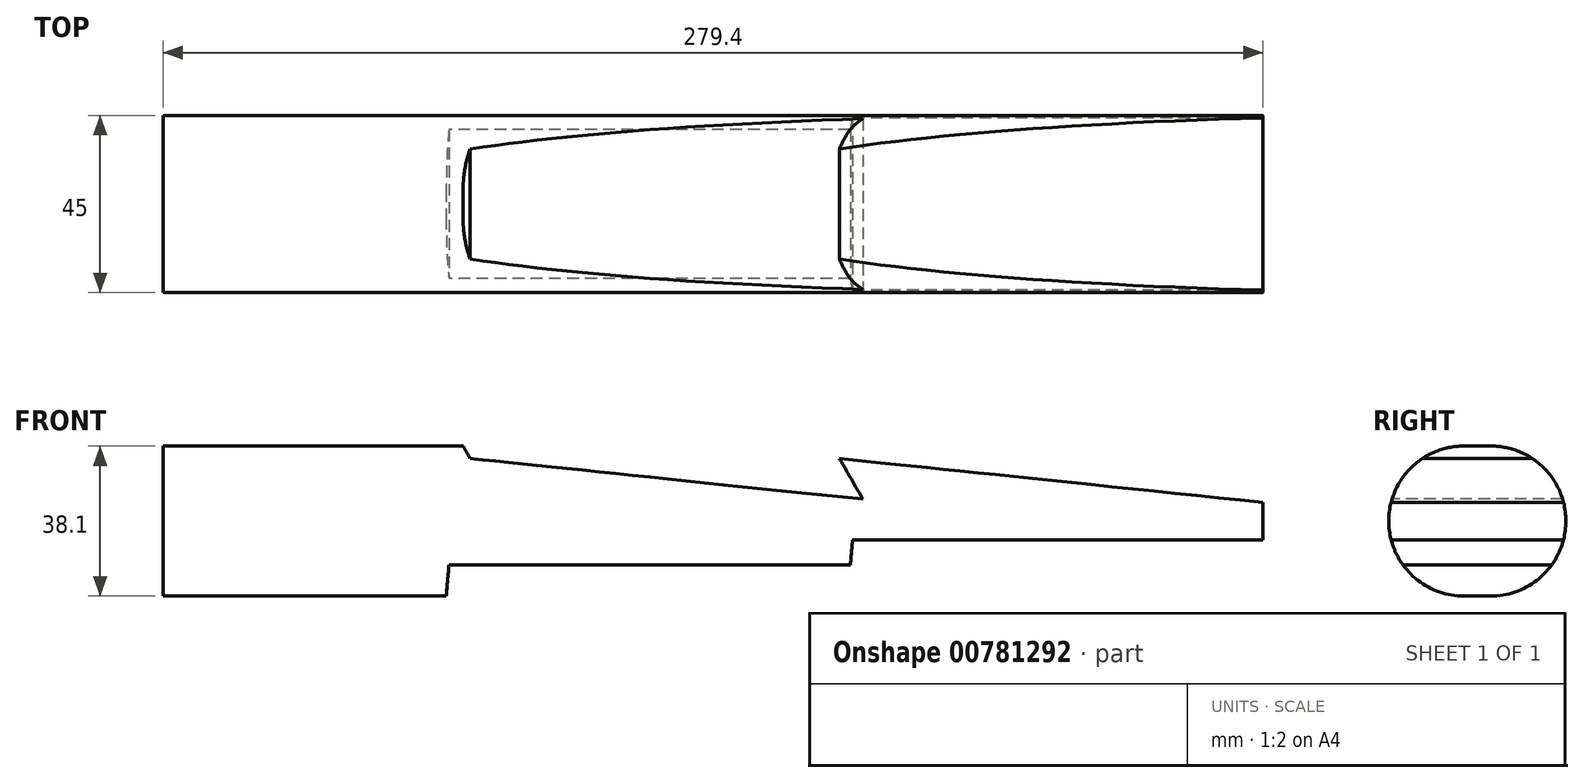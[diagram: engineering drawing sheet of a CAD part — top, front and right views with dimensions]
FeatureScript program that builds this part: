
annotation { "Feature Type Name" : "Feature", "Feature Type Description" : "" }
export const myFeature = defineFeature(function(context is Context, id is Id, definition is map)
    precondition{}
    {
        {
            var Q0;
            Q0=qCreatedBy(makeId("Right.planeOp"),FACE);
            var sketch = newSketch(context, id + "F0", { "sketchPlane" : qUnion([Q0])});
            skLineSegment(sketch, "E0", {"start": v(-3.45, 0) * mm, "end": v(3.45, 0) * mm});
            skArc(sketch, "E1.0.startCap", {"start": v(-3.45, -19.05) * mm, "mid": v(-22.5, 0) * mm, "end": v(-3.45, 19.05) * mm});
            skArc(sketch, "E1.0.endCap", {"start": v(3.45, 19.05) * mm, "mid": v(22.5, 0) * mm, "end": v(3.45, -19.05) * mm});
            skLineSegment(sketch, "E1.0.left", {"start": v(-3.45, 19.05) * mm, "end": v(3.45, 19.05) * mm});
            skLineSegment(sketch, "E1.0.right", {"start": v(-3.45, -19.05) * mm, "end": v(3.45, -19.05) * mm});
            skSolve(sketch);
        }
        {
            var Q0;
            Q0 = qSketchRegion(id + "F0", true);
            extrude(context, id + "F1", {"entities" : qUnion([Q0]), "depth" : 139.7 * mm, "offsetDistance" : 25.4 * mm, "hasSecondDirection" : true, "secondDirectionOppositeDirection" : true, "secondDirectionDepth" : 139.7 * mm});
        }
        {
            var Q0;
            Q0=qCreatedBy(makeId("Front.planeOp"),FACE);
            var sketch = newSketch(context, id + "F2", { "sketchPlane" : qUnion([Q0])});
            skLineSegment(sketch, "E2", {"start": v(-63.5, 19.05) * mm, "end": v(-61.67, 15.88) * mm});
            skLineSegment(sketch, "E3", {"start": v(38.1, 5.57) * mm, "end": v(32.15, 15.88) * mm});
            skLineSegment(sketch, "E4", {"start": v(139.7, 4.76) * mm, "end": v(139.7, 19.05) * mm});
            skLineSegment(sketch, "E5", {"start": v(139.7, 19.05) * mm, "end": v(-63.5, 19.05) * mm});
            skLineSegment(sketch, "E6", {"start": v(32.15, 15.88) * mm, "end": v(139.7, 4.76) * mm});
            skPoint(sketch, "E7.orphan", {"position": v(139.7, 15.88) * mm});
            skLineSegment(sketch, "E8", {"start": v(-61.67, 15.88) * mm, "end": v(38.1, 5.57) * mm});
            skSolve(sketch);
        }
        {
            var Q0;
            Q0 = qSketchRegion(id + "F2", true);
            extrude(context, id + "F3", {"entities" : qUnion([Q0]), "operationType" : NewBodyOperationType.REMOVE, "endBound" : BoundingType.THROUGH_ALL, "oppositeDirection" : true, "depth" : 25.4 * mm, "offsetDistance" : 25.4 * mm, "hasSecondDirection" : true, "secondDirectionBound" : SecondDirectionBoundingType.THROUGH_ALL, "secondDirectionOppositeDirection" : false, "secondDirectionDepth" : 25.4 * mm});
        }
        {
            var Q0;
            Q0=qCreatedBy(makeId("Front.planeOp"),FACE);
            var sketch = newSketch(context, id + "F4", { "sketchPlane" : qUnion([Q0])});
            skLineSegment(sketch, "E9", {"start": v(139.7, -4.76) * mm, "end": v(35.48, -4.76) * mm});
            skLineSegment(sketch, "E10", {"start": v(35.48, -4.76) * mm, "end": v(34.93, -11.11) * mm});
            skLineSegment(sketch, "E11", {"start": v(34.93, -11.11) * mm, "end": v(-67.06, -11.11) * mm});
            skLineSegment(sketch, "E12", {"start": v(-67.06, -11.11) * mm, "end": v(-67.76, -19.05) * mm});
            skLineSegment(sketch, "E13", {"start": v(-67.76, -19.05) * mm, "end": v(139.7, -19.05) * mm});
            skLineSegment(sketch, "E14", {"start": v(139.7, -19.05) * mm, "end": v(139.7, -4.76) * mm});
            skSolve(sketch);
        }
        {
            var Q0;
            Q0 = qSketchRegion(id + "F4", true);
            extrude(context, id + "F5", {"entities" : qUnion([Q0]), "operationType" : NewBodyOperationType.REMOVE, "endBound" : BoundingType.THROUGH_ALL, "oppositeDirection" : true, "depth" : 25.4 * mm, "offsetDistance" : 25.4 * mm, "hasSecondDirection" : true, "secondDirectionBound" : SecondDirectionBoundingType.THROUGH_ALL, "secondDirectionOppositeDirection" : false, "secondDirectionDepth" : 25.4 * mm});
        }
    });
